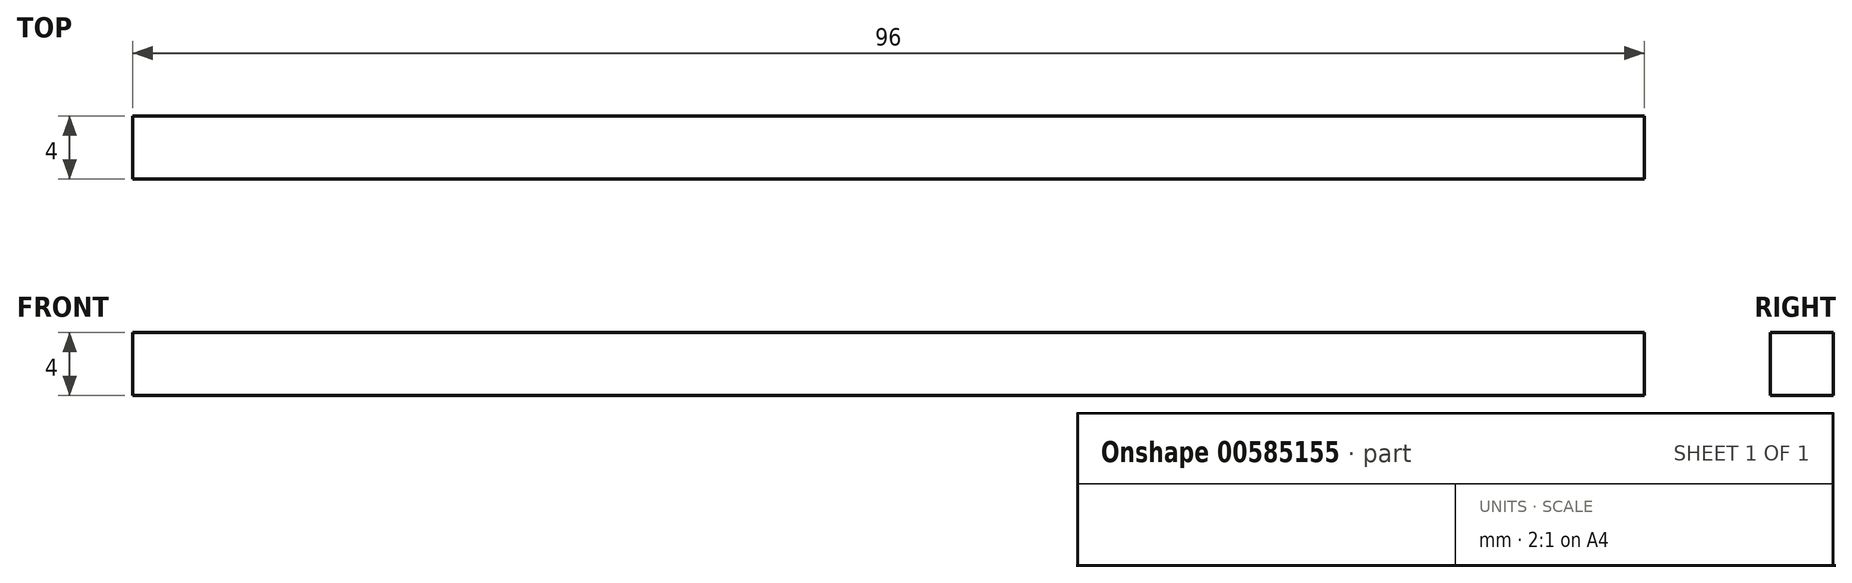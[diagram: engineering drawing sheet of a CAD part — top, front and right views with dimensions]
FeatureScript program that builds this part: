
annotation { "Feature Type Name" : "Feature", "Feature Type Description" : "" }
export const myFeature = defineFeature(function(context is Context, id is Id, definition is map)
    precondition{}
    {
        {
            var Q0;
            Q0=qCreatedBy(makeId("Top.planeOp"),FACE);
            var sketch = newSketch(context, id + "F0", { "sketchPlane" : qUnion([Q0])});
            skLineSegment(sketch, "E0.bottom", {"start": v(-43.24, 4) * mm, "end": v(52.76, 4) * mm});
            skLineSegment(sketch, "E0.top", {"start": v(-43.24, 0) * mm, "end": v(52.76, 0) * mm});
            skLineSegment(sketch, "E0.left", {"start": v(-43.24, 4) * mm, "end": v(-43.24, 0) * mm});
            skLineSegment(sketch, "E0.right", {"start": v(52.76, 4) * mm, "end": v(52.76, 0) * mm});
            skSolve(sketch);
        }
        {
            var Q0;
            Q0 = qSketchRegion(id + "F0", true);
            extrude(context, id + "F1", {"entities" : qUnion([Q0]), "depth" : 4 * mm, "offsetDistance" : 25 * mm});
        }
    });
